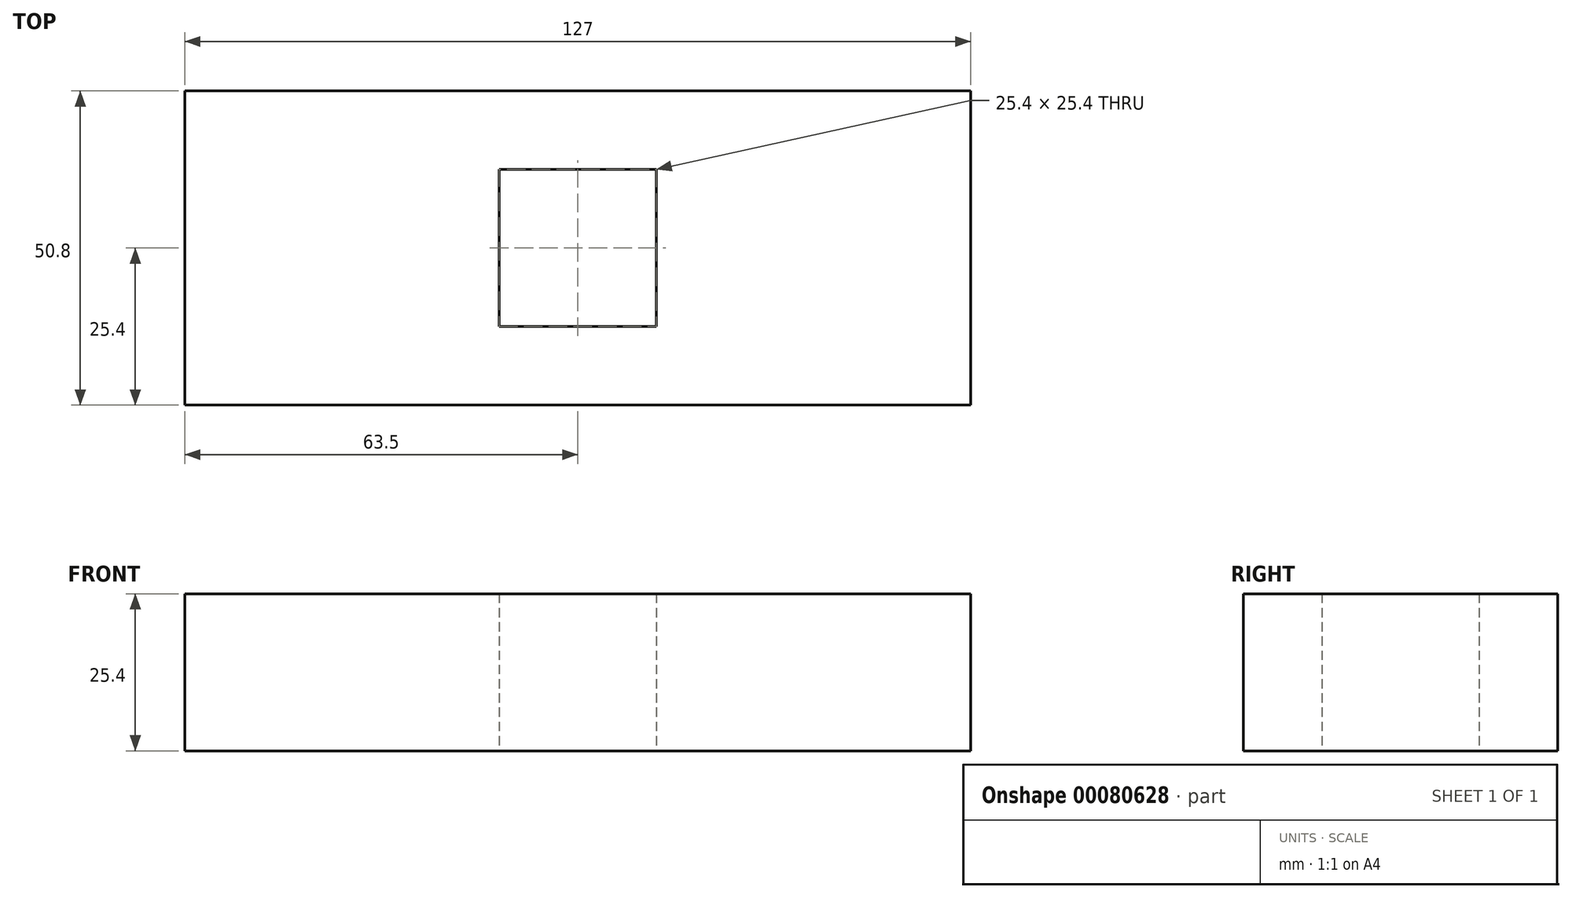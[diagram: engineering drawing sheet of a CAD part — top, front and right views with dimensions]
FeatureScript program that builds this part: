
annotation { "Feature Type Name" : "Feature", "Feature Type Description" : "" }
export const myFeature = defineFeature(function(context is Context, id is Id, definition is map)
    precondition{}
    {
        {
            var Q0;
            Q0=qCreatedBy(makeId("Top.planeOp"),FACE);
            var sketch = newSketch(context, id + "F0", { "sketchPlane" : qUnion([Q0])});
            skLineSegment(sketch, "E0.bottom", {"start": v(-63.5, 25.4) * mm, "end": v(63.5, 25.4) * mm});
            skLineSegment(sketch, "E0.top", {"start": v(-63.5, -25.4) * mm, "end": v(63.5, -25.4) * mm});
            skLineSegment(sketch, "E0.left", {"start": v(-63.5, 25.4) * mm, "end": v(-63.5, -25.4) * mm});
            skLineSegment(sketch, "E0.right", {"start": v(63.5, 25.4) * mm, "end": v(63.5, -25.4) * mm});
            skPoint(sketch, "E0.middle", {"position": v(0, 0) * mm});
            skLineSegment(sketch, "E1.bottom", {"start": v(-12.7, 12.7) * mm, "end": v(12.7, 12.7) * mm});
            skLineSegment(sketch, "E1.top", {"start": v(-12.7, -12.7) * mm, "end": v(12.7, -12.7) * mm});
            skLineSegment(sketch, "E1.left", {"start": v(-12.7, 12.7) * mm, "end": v(-12.7, -12.7) * mm});
            skLineSegment(sketch, "E1.right", {"start": v(12.7, 12.7) * mm, "end": v(12.7, -12.7) * mm});
            skSolve(sketch);
        }
        {
            var Q0;
            Q0=makeQuery(id+"F0.imprint","IMPRINT",FACE,{"disambiguationData":[TD([[makeQuery(id+"F0.imprint","IMPRINT",EDGE,{"derivedFrom":sQuery(id+"F0.wireOp",EDGE,"E0.bottom")}),-1.0]])]});
            extrude(context, id + "F1", {"entities" : qUnion([Q0]), "depth" : 25.4 * mm});
        }
    });
